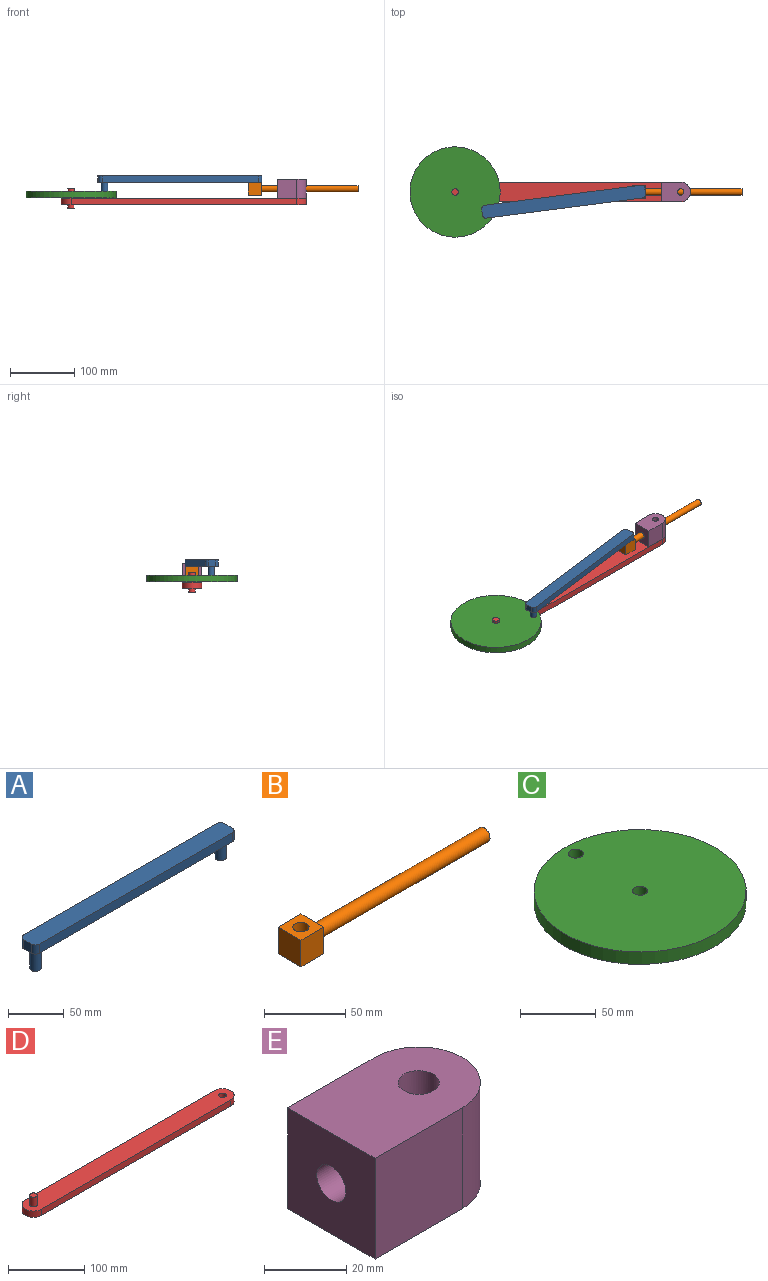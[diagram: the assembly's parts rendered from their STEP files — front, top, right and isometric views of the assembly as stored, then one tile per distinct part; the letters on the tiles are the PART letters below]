
ASSEMBLY  parts=5 mates=5
PART A: 14 faces, bbox 255x20x34 mm
  f0: plane 245x10mm, normal (0,-1,0), area 2450mm2, adj f4,f5,f6,f9
  f1: plane 10x10mm, normal (1,0,0), area 100mm2, adj f4,f5,f6,f7
  f2: plane 245x10mm, normal (0,1,0), area 2450mm2, adj f4,f5,f7,f8
  f3: plane 10x10mm, normal (-1,0,0), area 100mm2, adj f4,f5,f8,f9
  f4: plane 255x20mm, normal (0,0,1), area 5078.5mm2, adj f0,f1,f2,f3,f6,f7,f8,f9
  f5: plane 255x20mm, normal (0,0,-1), area 4921.5mm2, adj f0,f1,f2,f3,f6,f7,f8,f9
  f6: cylinder r=5mm len=10mm, axis (0,0,-1), area 78.5mm2, adj f0,f1,f4,f5
  f7: cylinder r=5mm len=10mm, axis (0,0,1), area 78.5mm2, adj f1,f2,f4,f5
  f8: cylinder r=5mm len=10mm, axis (0,0,-1), area 78.5mm2, adj f2,f3,f4,f5
  f9: cylinder r=5mm len=10mm, axis (0,0,1), area 78.5mm2, adj f0,f3,f4,f5
  f10: plane 10x10mm, normal (0,0,-1), area 78.5mm2, adj f11
  f11: cylinder r=5mm len=20mm, axis (0,0,1), area 628.3mm2, adj f5,f10
  f12: plane 10x10mm, normal (0,0,-1), area 78.5mm2, adj f13
  f13: cylinder r=5mm len=24mm, axis (0,0,1), area 754mm2, adj f5,f12
PART B: 9 faces, bbox 170x20x20 mm
  f0: cylinder r=5mm len=150mm, axis (-1,0,0), area 4712.4mm2, adj f1,f7
  f1: plane 10x10mm, normal (1,0,0), area 78.5mm2, adj f0
  f2: plane 20x20mm, normal (0,-1,0), area 400mm2, adj f3,f5,f6,f7
  f3: plane 20x20mm, normal (0,0,1), area 321.5mm2, adj f2,f4,f6,f7,f8
  f4: plane 20x20mm, normal (0,1,0), area 400mm2, adj f3,f5,f6,f7
  f5: plane 20x20mm, normal (0,0,-1), area 321.5mm2, adj f2,f4,f6,f7,f8
  f6: plane 20x20mm, normal (-1,0,0), area 400mm2, adj f2,f3,f4,f5
  f7: plane 20x20mm, normal (1,0,0), area 321.5mm2, adj f0,f2,f3,f4,f5
  f8: cylinder r=5mm len=20mm, axis (0,0,1), area 628.3mm2, adj f3,f5
PART C: 5 faces, bbox 140x140x10 mm
  f0: cylinder r=5mm len=10mm, axis (0,0,-1), area 314.2mm2, adj f3,f4
  f1: cylinder r=5mm len=10mm, axis (0,0,-1), area 314.2mm2, adj f3,f4
  f2: cylinder r=70mm len=140mm, axis (0,0,-1), area 4398.2mm2, adj f3,f4
  f3: plane 140x140mm, normal (0,0,1), area 15236.7mm2, adj f0,f1,f2
  f4: plane 140x140mm, normal (0,0,-1), area 15236.7mm2, adj f0,f1,f2
PART D: 11 faces, bbox 380x30x30 mm
  f0: cylinder r=15mm len=30mm, axis (0,0,1), area 471.2mm2, adj f1,f4,f5,f6
  f1: plane 350x10mm, normal (0,-1,0), area 3500mm2, adj f0,f2,f5,f6
  f2: cylinder r=15mm len=30mm, axis (0,0,1), area 471.2mm2, adj f1,f4,f5,f6
  f3: cylinder r=5mm len=10mm, axis (0,0,1), area 314.2mm2, adj f5,f6
  f4: plane 350x10mm, normal (0,1,0), area 3500mm2, adj f0,f2,f5,f6
  f5: plane 380x30mm, normal (0,0,-1), area 11049.8mm2, adj f0,f1,f2,f3,f4,f9
  f6: plane 380x30mm, normal (0,0,1), area 11049.8mm2, adj f0,f1,f2,f3,f4,f8
  f7: plane 10x10mm, normal (0,0,1), area 78.5mm2, adj f8
  f8: cylinder r=5mm len=15mm, axis (0,0,-1), area 471.2mm2, adj f6,f7
  f9: cylinder r=5mm len=10mm, axis (0,0,-1), area 157.1mm2, adj f5,f10
  f10: plane 10x10mm, normal (0,0,-1), area 78.5mm2, adj f9
PART E: 10 faces, bbox 45x30x30 mm
  f0: cylinder r=5mm len=15mm, axis (0,0,-1), area 371.2mm2, adj f7,f8,f9
  f1: plane 30x30mm, normal (0,-1,0), area 900mm2, adj f2,f4,f6,f7
  f2: cylinder r=15mm len=30mm, axis (0,0,-1), area 1334.1mm2, adj f1,f3,f6,f7,f9
  f3: plane 30x30mm, normal (0,1,0), area 900mm2, adj f2,f4,f6,f7
  f4: plane 30x30mm, normal (-1,0,0), area 821.5mm2, adj f1,f3,f6,f7,f8
  f5: cylinder r=5mm len=15mm, axis (0,0,-1), area 371.2mm2, adj f6,f8,f9
  f6: plane 45x30mm, normal (0,0,1), area 1174.9mm2, adj f1,f2,f3,f4,f5
  f7: plane 45x30mm, normal (0,0,-1), area 1174.9mm2, adj f0,f1,f2,f3,f4
  f8: cylinder r=5mm len=30mm, axis (-1,0,0), area 842.5mm2, adj f0,f4,f5
  f9: cylinder r=5mm len=15mm, axis (-1,0,0), area 357.8mm2, adj f0,f2,f5
PLACE A rot(axis=(0,0,1),7.3deg) t=(-7.51,-37.57,0)mm
PLACE B t=(4.99,0,0)mm
PLACE C rot(axis=(0,0,-1),119.9deg) t=(0,0,16)mm
PLACE D t=(0,0,15)mm
PLACE E at identity
MATE slider B.f0 <-> E.f8  axis (1,0,0) through (444.99,0,30)mm
MATE fastened D.f0 <-> E.f0  axis (0,0,1) through (350,0,15)mm
MATE revolute A.f11 <-> B.f8  axis (0,0,-1) through (284.99,0,20)mm
MATE revolute A.f13 <-> C.f1  axis (0,0,-1) through (52,-29.93,16)mm
MATE revolute C.f2 <-> D.f8  axis (0,0,1) through (0,0,26)mm
